# Revit family: Hager-VEGAD-Surface_mounted-IP30-Without_Cover-With_DIN-Hosted-ES-es
name_source: partatom
category: Electrical Equipment
units: mm (PartAtom-declared; Revit-internal decimal feet)

## family parameters
Cut with Voids When Loaded = No
Host = Face
Maintain Annotation Orientation = Yes
Panel Configuration = Two Columns, Circuits Across
Part Type = Panelboard
Room Calculation Point = No
Round Connector Dimension = Use Diameter
Shared = No

## types (10) — shared parameters
BC_MODEL_ID = 1547011
BC_OBJECT_ID = 513437
BC_OBJECT_VERSION = #3
Code hager = ADD-EC000214_EU
EF000003 - Método de montaje = Montado superficial (escayola)
EF000007 - Color = Blanco
EF000008 - Anchura = 550 mm  [stored 1.80446 ft]
EF000024 - Resistente a UV = No
EF000049 - Profundidad = 193 mm  [stored 0.633202 ft]
EF000116 - Número RAL = 9010
EF000118 - Con placa de montaje = No
EF000218 - Profundidad de instalación = 193 mm  [stored 0.633202 ft]
EF000846 - Anchura de montaje = 550 mm  [stored 1.80446 ft]
EF001062 - Versión de CEM = No
EF001088 - Posibilidad de extensión = Yes
EF001134 - Carril DIN = Yes
EF002950 - Ancho en número de espacios modulares = 24
EF005474 - Grado de protección (IP) = IP30
EF006244 - Tapa/puerta transparente = No
EF006306 - Con candado = No
EF009212 - Versión de la cubierta = Con muesca
EF015776 - Borne de tierra = Yes
EF015777 - Borne neutro = No
EF015941 - Puerta de transmisión de señal = No
ETIM class code = EC000214
ETIM class name = Small distribution board
HG000001 - Número de columnas = 1
HG000002-with door or cover-es = No
HG000003-Range-es = VEGAD
HG000005-Thickness-es = 2 mm  [stored 0.00656168 ft]
HG000006-Flush mounted-es = No
HG000009-Double swing door-es = No
HG000010-Asymmetric doors-es = No
HG000011-Empty rows from bottom-es = No
HG000012-Door swing angle-es = 90.00°
HG000013-Door on the left-es = No
HG000014-Door on the right-es = Yes
HG000015-Clearance visibility-es = Yes
HG000016-Door 3D visibility-es = Yes
HG000017-Distance between poles-es = 18 mm  [stored 0.0590551 ft]
HG000060-RAL-number = 9010
HG000099-Onfly Template ID-es-ES = 507532
HGEF0002950-Ancho en número de espacios modulares = 24
Manufacturer = Hager
Name = VEGAD-Surface_mounted-IP30-Without_Cover-With_DIN-ES
Name BIM&CO = Electricity
Name hager = ADD_Enclosures_EC000214
Uniformat = Low Tension Service & Dist.
Uniformat code = D501001
zero-valued in all types: Default Elevation, EF001131 - Profundidad interna, HG000007-Number of empty columns-es

## per-type parameters (varying)
| type | BC_VARIANT_ID | EF000040 - Altura | EF000266 - Número de filas | EF000332 - Altura de la instalación | HG000004-Manufacturer reference-es | HG000008-Number of empty rows-es | HGEF000266-Número de filas |
| VEGAD-Surface_mounted_W550_H450_D193_24_Modular_Spacing-FD22DN | 1173893 | 450 mm  [stored 1.47638 ft] | 2 | 450 mm  [stored 1.47638 ft] | FD22DN | 0 | 2 |
| VEGAD-Surface_mounted_W550_H600_D193_24_Modular_Spacing-FD32DN | 1173894 | 600 mm | 3 | 600 mm | FD32DN | 0 | 3 |
| VEGAD-Surface_mounted_W550_H750_D193_24_Modular_Spacing-FD42AN | 1173895 | 750 mm  [stored 2.46063 ft] | 4 | 750 mm  [stored 2.46063 ft] | FD42AN | 2 | 4 |
| VEGAD-Surface_mounted_W550_H750_D193_24_Modular_Spacing-FD42DN | 1173896 | 750 mm  [stored 2.46063 ft] | 4 | 750 mm  [stored 2.46063 ft] | FD42DN | 0 | 4 |
| VEGAD-Surface_mounted_W550_H900_D193_24_Modular_Spacing-FD52AN | 1173897 | 900 mm  [stored 2.95276 ft] | 5 | 900 mm  [stored 2.95276 ft] | FD52AN | 2 | 5 |
| VEGAD-Surface_mounted_W550_H900_D193_24_Modular_Spacing-FD52DN | 1173898 | 900 mm  [stored 2.95276 ft] | 5 | 900 mm  [stored 2.95276 ft] | FD52DN | 0 | 5 |
| VEGAD-Surface_mounted_W550_H1050_D193_24_Modular_Spacing-FD62AN | 1173899 | 1050 mm | 6 | 1050 mm | FD62AN | 2 | 6 |
| VEGAD-Surface_mounted_W550_H1050_D193_24_Modular_Spacing-FD62DN | 1173900 | 1050 mm | 6 | 1050 mm | FD62DN | 0 | 6 |
| VEGAD-Surface_mounted_W550_H1200_D193_24_Modular_Spacing-FD72AN | 1173901 | 1200 mm  [stored 3.93701 ft] | 7 | 1200 mm  [stored 3.93701 ft] | FD72AN | 2 | 7 |
| VEGAD-Surface_mounted_W550_H1200_D193_24_Modular_Spacing-FD72DN | 1173902 | 1200 mm  [stored 3.93701 ft] | 7 | 1200 mm  [stored 3.93701 ft] | FD72DN | 0 | 7 |

note: column(s) folded — value = type name in every type: Reference

note: [stored X ft] marks values corroborated as IEEE doubles in the binary element streams (Revit-internal decimal feet)

## geometry (parser evidence)
native form markers: Sweep x16
no freeform markers — native parametric forms only
